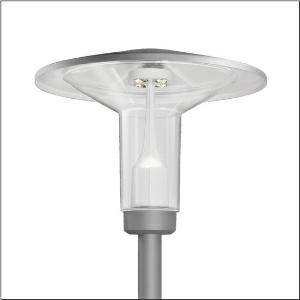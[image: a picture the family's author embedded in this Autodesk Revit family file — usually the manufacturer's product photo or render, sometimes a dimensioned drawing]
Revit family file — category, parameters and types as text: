
# Revit family: laterne_iq___p1_0a_5xa5255nf14h_4412
name_source: partatom
category: Lighting Fixtures
units: mm (PartAtom-declared; Revit-internal decimal feet)

## family parameters
Cut with Voids When Loaded = No
Host = Face
Light Source = No
Part Type = Normal
Room Calculation Point = No
Round Connector Dimension = Use Diameter
Shared = No

## types (1)
- --- (1 x LED, 1510 lm, 11.8 W, 2700K)
    Apparent Load = 12 VA
    CIE Flux Codes = 35 64 91 96 100
    Color Rendering = 70
    Color Temperature = 2700K
    Default Elevation = 1800 mm
    Description = Lantern iQ, mast luminaire, Module 540 iQ-SR, primary light control with 3 zone facetted reflector, of plastic, silver coated, highly specular, structured, primary optical cover: cover, of PMMA, transparent, light distribution: P1.0a, light emission: direct distribution, primary light characteristic: strongly asymmetric, installation type: post-top, LED, High Power LED, rated luminous flux: 1.510lm, luminous efficacy: 128lm/W, light colour: 727, colour temperature: 2700K, control gear: ECG iQ, control: presetting dimming logarithmic, Street-Remote, Auto-Match, Temp-Guard, Lumen-Switch, Night-Set, Smart-Wire, Light-Fading, Desk-Remote (wireless, voltage-free reading and setting of iQ features in the workshop via application-optimized NFC function/RFID function), optimised constant luminous flux control (CLO 2.0), with terminal, 6-pole, max. 2.5mm², mains connection: 230..240V, AC, 50/60Hz, start of lifetime: 12W, end of service life: 12W, reduction: 6W, luminaire housing, upper part, of glass-fibre reinforced polyester, coated, Siteco® metallic grey (DB 702S), diameter: 750mm, height: 583mm, spigot size: d x l = 76 x 70mm (post-top) | with reducer (optional accessory) 60 x 70mm, post-top mast mounting element, of diecast aluminium, coated, Siteco® metallic grey (DB 702S), Module 540 iQ-SR, traffic white (RAL 9016), equipment: standard, protection rating (complete): IP65, insulation class (complete): insulation class II (safety insulation), certification: CE, ENEC, VDE, packaging unit: 1 piece

Light Distribution: P1.0a
    Height = 583 mm
    Lamp = 1 x LED
    Lamp Light Flux = 1510 lm
    Lamp Power = 11.8 W
    Lamp count = 1
    Length = 750 mm
    Luminous efficacy = 128 lm/W
    Manufacturer = Siteco
    ModVariant = No
    Model = 5XA5255NF14H
    Number of Poles = 1
    OnlyDefault = Yes
    Power Factor = 1
    Product Name = Laterne iQ | P1.0a
    Product group = mast luminaire | pylon top
    ProductGroupID = 6100
    Protection Class = Protection class II
    Protection Degree = IP 65
    RLX_Detail_Level = 1
    RLX_Emergency_Light_Flux = 0 lm
    RLX_Emergency_Type = 0
    RLX_Emergency_Type_DB = No
    RlxData = <blob elided: 73837 chars, md5=e6f57035>
    Socket = socket
    Standby Power = 0 W
    System Light Flux = 1510 lm
    System Power = 12 W
    Type Comments = factory setting: luminous flux: 100 % | dim-lin: 254 | 472 mA
    Type Image = l_1006050.jpg
    URL = http://relux.com
    VarID = @adj_085679
    Voltage = 0 V
    Weight = 0.00 kg
    Width = 0 mm  [stored 0 ft]

note: [stored X ft] marks values corroborated as IEEE doubles in the binary element streams (Revit-internal decimal feet)

## geometry (parser evidence)
native form markers: Blend x4, Sweep x10
no freeform markers — native parametric forms only
